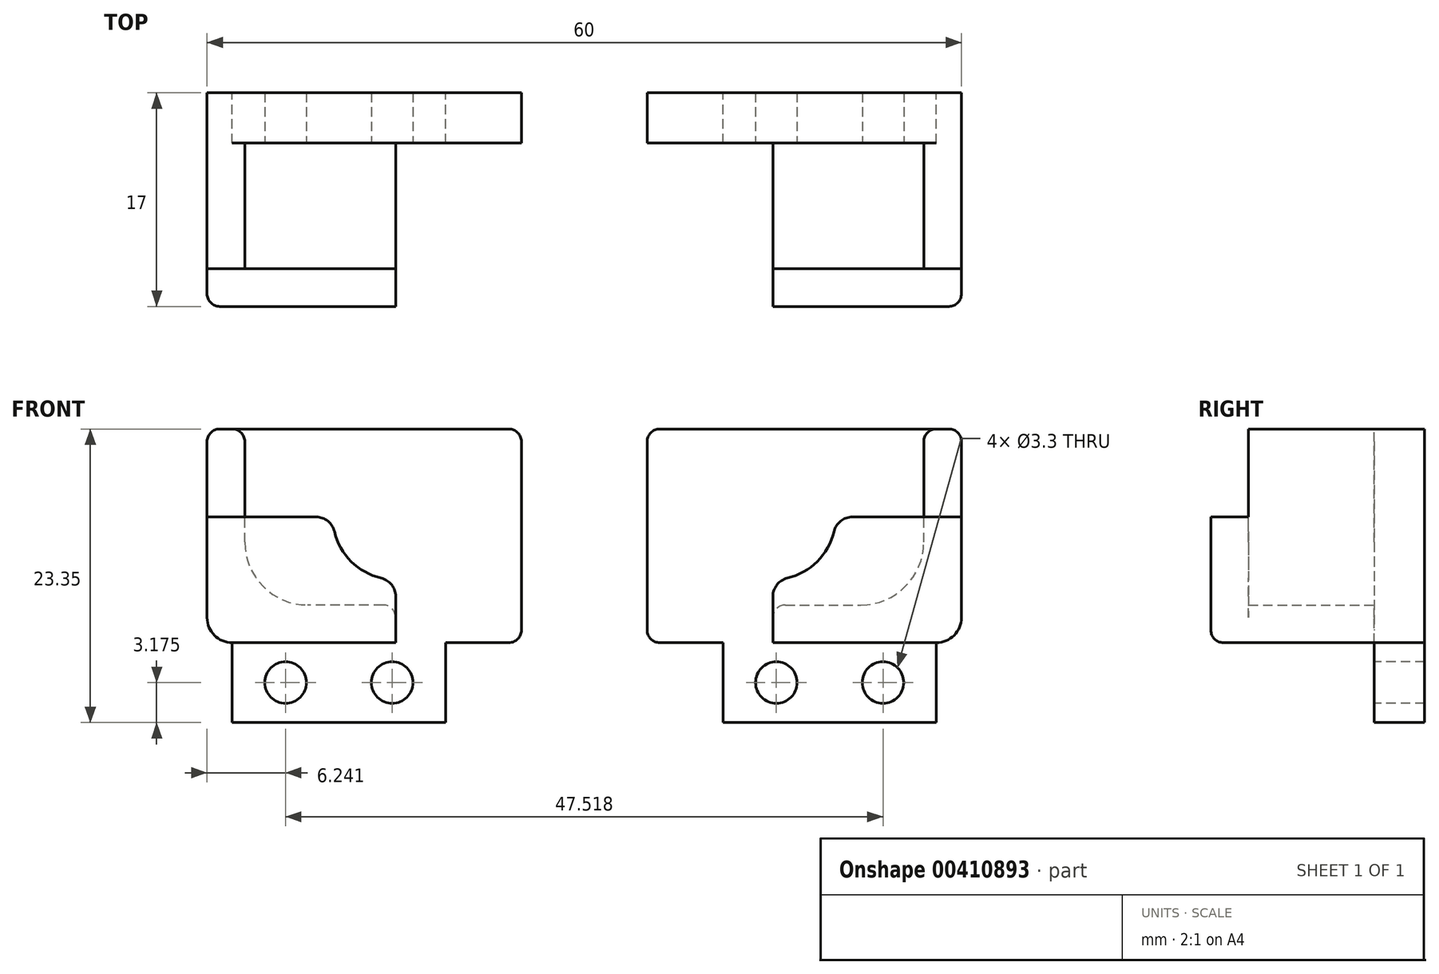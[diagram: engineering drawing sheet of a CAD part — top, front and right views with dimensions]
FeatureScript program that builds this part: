
annotation { "Feature Type Name" : "Feature", "Feature Type Description" : "" }
export const myFeature = defineFeature(function(context is Context, id is Id, definition is map)
    precondition{}
    {
        {
            var Q0;
            Q0=qCreatedBy(makeId("Top.planeOp"),FACE);
            var sketch = newSketch(context, id + "F0", { "sketchPlane" : qUnion([Q0])});
            skLineSegment(sketch, "E0.bottom", {"start": v(-25, 17) * mm, "end": v(0, 17) * mm});
            skLineSegment(sketch, "E0.top", {"start": v(-25, 0) * mm, "end": v(0, 0) * mm});
            skLineSegment(sketch, "E0.left", {"start": v(-25, 17) * mm, "end": v(-25, 0) * mm});
            skLineSegment(sketch, "E0.right", {"start": v(0, 17) * mm, "end": v(0, 0) * mm});
            skSolve(sketch);
        }
        {
            var Q0;
            Q0=makeQuery(id+"F0.imprint","IMPRINT",FACE,{"disambiguationData":[TD([[makeQuery(id+"F0.imprint","IMPRINT",EDGE,{"derivedFrom":sQuery(id+"F0.wireOp",EDGE,"E0.bottom")}),-1.0]])]});
            extrude(context, id + "F1", {"entities" : qUnion([Q0]), "depth" : 4 * mm});
        }
        {
            var Q0;
            Q0=makeQuery(id+"F1.opExtrude","CAP_FACE",FACE,{"disambiguationData":[OSD([sQuery(id+"F0.wireOp",EDGE,"E0.bottom"),sQuery(id+"F0.wireOp",EDGE,"E0.top"),sQuery(id+"F0.wireOp",EDGE,"E0.left"),sQuery(id+"F0.wireOp",EDGE,"E0.right")])],"isStart":false});
            var sketch = newSketch(context, id + "F2", { "sketchPlane" : qUnion([Q0])});
            skLineSegment(sketch, "E1", {"start": v(-25, 17) * mm, "end": v(-25, 0) * mm});
            skLineSegment(sketch, "E2", {"start": v(-25, 0) * mm, "end": v(-10, 0) * mm});
            skLineSegment(sketch, "E3", {"start": v(-10, 0) * mm, "end": v(-10, 3) * mm});
            skLineSegment(sketch, "E4", {"start": v(-10, 3) * mm, "end": v(-22, 3) * mm});
            skLineSegment(sketch, "E5", {"start": v(-22, 3) * mm, "end": v(-22, 17) * mm});
            skLineSegment(sketch, "E6", {"start": v(-22, 17) * mm, "end": v(-25, 17) * mm});
            skSolve(sketch);
        }
        {
            var Q0;
            Q0=makeQuery(id+"F2.imprint","IMPRINT",FACE,{"disambiguationData":[TD([[makeQuery(id+"F2.imprint","IMPRINT",EDGE,{"derivedFrom":sQuery(id+"F2.wireOp",EDGE,"E1")}),1.0]])]});
            extrude(context, id + "F3", {"entities" : qUnion([Q0]), "operationType" : NewBodyOperationType.ADD, "depth" : 10 * mm});
        }
        {
            var Q0;
            Q0=makeQuery(id+"F3.opExtrude","CAP_FACE",FACE,{"disambiguationData":[OSD([sQuery(id+"F2.wireOp",EDGE,"E1"),sQuery(id+"F2.wireOp",EDGE,"E2"),sQuery(id+"F2.wireOp",EDGE,"E3"),sQuery(id+"F2.wireOp",EDGE,"E4"),sQuery(id+"F2.wireOp",EDGE,"E5"),sQuery(id+"F2.wireOp",EDGE,"E6")])],"isStart":false});
            var sketch = newSketch(context, id + "F4", { "sketchPlane" : qUnion([Q0])});
            skLineSegment(sketch, "E7.bottom", {"start": v(-25, 10) * mm, "end": v(-16.32, 10) * mm});
            skLineSegment(sketch, "E7.top", {"start": v(-25, 0) * mm, "end": v(-10, 0) * mm});
            skLineSegment(sketch, "E7.left", {"start": v(-25, 10) * mm, "end": v(-25, 0) * mm});
            skLineSegment(sketch, "E7.right", {"start": v(-10, 10) * mm, "end": v(-10, 5) * mm, "construction": true});
            skArc(sketch, "E8", {"start": v(-14.87, 8.85) * mm, "mid": v(-13.54, 6.46) * mm, "end": v(-11.15, 5.13) * mm});
            skLineSegment(sketch, "E9", {"start": v(-15, 10) * mm, "end": v(-10, 10) * mm, "construction": true});
            skLineSegment(sketch, "E10", {"start": v(-10, 3.68) * mm, "end": v(-10, 0) * mm});
            skPoint(sketch, "E11.visualSharp", {"position": v(-15, 10) * mm});
            skArc(sketch, "E11.filletArc", {"start": v(-14.87, 8.85) * mm, "mid": v(-15.4, 9.68) * mm, "end": v(-16.32, 10) * mm});
            skPoint(sketch, "E12.visualSharp", {"position": v(-10, 5) * mm});
            skArc(sketch, "E12.filletArc", {"start": v(-10, 3.68) * mm, "mid": v(-10.32, 4.6) * mm, "end": v(-11.15, 5.13) * mm});
            skSolve(sketch);
        }
        {
            var Q0;
            {var subQ1=makeQuery(id+"F3.opExtrude","CAP_EDGE",EDGE,{"disambiguationData":[OSD([sQuery(id+"F2.wireOp",EDGE,"E4")])],"isStart":false});Q0=makeQuery(id+"F4.imprint","IMPRINT",FACE,{"disambiguationData":[TD([[makeQuery(id+"F4.imprint","IMPRINT",EDGE,{"derivedFrom":subQ1}),-1.0]])]});}
            var Q1;
            {var subQ4=sQuery(id+"F4.wireOp",EDGE,"E7.top");Q1=makeQuery(id+"F4.imprint","IMPRINT",FACE,{"disambiguationData":[TD([[makeQuery(id+"F4.imprint","IMPRINT",EDGE,{"derivedFrom":subQ4}),1.0]])]});}
            extrude(context, id + "F5", {"entities" : qUnion([Q0, Q1]), "operationType" : NewBodyOperationType.ADD, "depth" : 3 * mm});
        }
        {
            var Q0;
            Q0=makeQuery(id+"F3.opExtrude","SWEPT_EDGE",EDGE,{"disambiguationData":[OSD([sQuery(id+"F2.wireOp",EDGE,"E4"),sQuery(id+"F2.wireOp",EDGE,"E5")])]});
            fillet(context, id + "F6", {"entities" : qUnion([Q0]), "radius" : 5 * mm, "tangentPropagation" : true, "allowEdgeOverflow" : false});
        }
        {
            var Q0;
            Q0=makeQuery(id+"F1.opExtrude","SWEPT_BODY",BODY,{"disambiguationData":[OSD([sQuery(id+"F0.wireOp",EDGE,"E0.bottom"),sQuery(id+"F0.wireOp",EDGE,"E0.top"),sQuery(id+"F0.wireOp",EDGE,"E0.left"),sQuery(id+"F0.wireOp",EDGE,"E0.right")])]});
            var Q1;
            Q1=makeQuery(id+"F1.opExtrude","CAP_EDGE",EDGE,{"disambiguationData":[OSD([sQuery(id+"F0.wireOp",EDGE,"E0.top")])],"isStart":true});
            transform(context, id + "F7", {"entities" : qUnion([Q0]), "transformType" : TransformType.ROTATION, "transformAxis" : qUnion([Q1]), "angle" : 90 * degree, "makeCopy" : false});
        }
        {
            var Q0;
            Q0=makeQuery(id+"F1.opExtrude","SWEPT_EDGE",EDGE,{"disambiguationData":[OSD([sQuery(id+"F0.wireOp",EDGE,"E0.bottom"),sQuery(id+"F0.wireOp",EDGE,"E0.right")])]});
            var Q1;
            Q1=makeQuery(id+"F1.opExtrude","SWEPT_EDGE",EDGE,{"disambiguationData":[OSD([sQuery(id+"F0.wireOp",EDGE,"E0.top"),sQuery(id+"F0.wireOp",EDGE,"E0.right")])]});
            var Q2;
            Q2=makeQuery(id+"F5.opExtrude","SWEPT_EDGE",EDGE,{"disambiguationData":[OSD([sQuery(id+"F4.wireOp",EDGE,"E7.bottom"),sQuery(id+"F4.wireOp",EDGE,"E7.right")])]});
            var Q3;
            Q3=makeQuery(id+"F3.boolean.opBoolean","MERGE",EDGE,{"derivedFrom":[makeQuery(id+"F1.opExtrude","SWEPT_EDGE",EDGE,{"disambiguationData":[OSD([sQuery(id+"F0.wireOp",EDGE,"E0.bottom"),sQuery(id+"F0.wireOp",EDGE,"E0.left")])]}),makeQuery(id+"F3.opExtrude","SWEPT_EDGE",EDGE,{"disambiguationData":[OSD([sQuery(id+"F2.wireOp",EDGE,"E1"),sQuery(id+"F2.wireOp",EDGE,"E6")])]})]});
            var Q4;
            Q4=makeQuery(id+"F3.opExtrude","SWEPT_EDGE",EDGE,{"disambiguationData":[OSD([sQuery(id+"F0.wireOp",EDGE,"E0.bottom"),sQuery(id+"F2.wireOp",EDGE,"E5"),sQuery(id+"F2.wireOp",EDGE,"E6")])]});
            var Q5;
            Q5=makeQuery(id+"F3.opExtrude","SWEPT_EDGE",EDGE,{"disambiguationData":[OSD([sQuery(id+"F2.wireOp",EDGE,"E3"),sQuery(id+"F2.wireOp",EDGE,"E4")])]});
            var Q6;
            Q6=makeQuery(id+"F5.opExtrude","CAP_EDGE",EDGE,{"disambiguationData":[OSD([sQuery(id+"F4.wireOp",EDGE,"E7.left")])],"isStart":false});
            var Q7;
            Q7=makeQuery(id+"F5.opExtrude","CAP_EDGE",EDGE,{"disambiguationData":[OSD([sQuery(id+"F4.wireOp",EDGE,"E7.top")])],"isStart":false});
            fillet(context, id + "F8", {"entities" : qUnion([Q0, Q1, Q2, Q3, Q4, Q5, Q6, Q7]), "radius" : 1 * mm, "tangentPropagation" : true, "allowEdgeOverflow" : false});
        }
        {
            var Q0;
            Q0=makeQuery(id+"F5.boolean.opBoolean","MERGE",EDGE,{"derivedFrom":[makeQuery(id+"F3.boolean.opBoolean","MERGE",EDGE,{"derivedFrom":[makeQuery(id+"F1.opExtrude","SWEPT_EDGE",EDGE,{"disambiguationData":[OSD([sQuery(id+"F0.wireOp",EDGE,"E0.top"),sQuery(id+"F0.wireOp",EDGE,"E0.left")])]}),makeQuery(id+"F3.opExtrude","SWEPT_EDGE",EDGE,{"disambiguationData":[OSD([sQuery(id+"F2.wireOp",EDGE,"E1"),sQuery(id+"F2.wireOp",EDGE,"E2")])]})]}),makeQuery(id+"F5.opExtrude","SWEPT_EDGE",EDGE,{"disambiguationData":[OSD([sQuery(id+"F4.wireOp",EDGE,"E7.top"),sQuery(id+"F4.wireOp",EDGE,"E7.left")])]})]});
            fillet(context, id + "F9", {"entities" : qUnion([Q0]), "radius" : 2 * mm, "tangentPropagation" : true, "allowEdgeOverflow" : false});
        }
        {
            var Q0;
            Q0=makeQuery(id+"F1.opExtrude","SWEPT_BODY",BODY,{"disambiguationData":[OSD([sQuery(id+"F0.wireOp",EDGE,"E0.bottom"),sQuery(id+"F0.wireOp",EDGE,"E0.top"),sQuery(id+"F0.wireOp",EDGE,"E0.left"),sQuery(id+"F0.wireOp",EDGE,"E0.right")])]});
            var Q1;
            Q1=qCreatedBy(makeId("Right.planeOp"),FACE);
            transform(context, id + "F10", {"entities" : qUnion([Q0]), "transformType" : TransformType.TRANSLATION_DISTANCE, "transformDirection" : qUnion([Q1]), "distance" : 5 * mm, "oppositeDirection" : true, "makeCopy" : false});
        }
        {
            var Q0;
            Q0=makeQuery(id+"F5.boolean.opBoolean","MERGE",FACE,{"derivedFrom":[makeQuery(id+"F3.boolean.opBoolean","MERGE",FACE,{"derivedFrom":[makeQuery(id+"F1.opExtrude","SWEPT_FACE",FACE,{"disambiguationData":[OSD([sQuery(id+"F0.wireOp",EDGE,"E0.top")])]}),makeQuery(id+"F3.opExtrude","SWEPT_FACE",FACE,{"disambiguationData":[OSD([sQuery(id+"F2.wireOp",EDGE,"E2")])]})]}),makeQuery(id+"F5.opExtrude","SWEPT_FACE",FACE,{"disambiguationData":[OSD([sQuery(id+"F4.wireOp",EDGE,"E7.top")])]})]});
            var sketch = newSketch(context, id + "F11", { "sketchPlane" : qUnion([Q0])});
            skLineSegment(sketch, "E13.bottom", {"start": v(-11.04, 0) * mm, "end": v(-28, 0) * mm});
            skLineSegment(sketch, "E13.top", {"start": v(-11.04, 4) * mm, "end": v(-28, 4) * mm});
            skLineSegment(sketch, "E13.right", {"start": v(-28, 0) * mm, "end": v(-28, 4) * mm});
            skLineSegment(sketch, "E14", {"start": v(-11.04, 4) * mm, "end": v(-11.04, 0) * mm});
            skSolve(sketch);
        }
        {
            var Q0;
            Q0 = qSketchRegion(id + "F11", true);
            extrude(context, id + "F12", {"entities" : qUnion([Q0]), "operationType" : NewBodyOperationType.ADD, "depth" : 6.35 * mm});
        }
        {
            var Q0;
            Q0=makeQuery(id+"F12.boolean.opBoolean","MERGE",FACE,{"derivedFrom":[makeQuery(id+"F1.opExtrude","CAP_FACE",FACE,{"disambiguationData":[OSD([sQuery(id+"F0.wireOp",EDGE,"E0.bottom"),sQuery(id+"F0.wireOp",EDGE,"E0.top"),sQuery(id+"F0.wireOp",EDGE,"E0.left"),sQuery(id+"F0.wireOp",EDGE,"E0.right")])],"isStart":false}),makeQuery(id+"F12.opExtrude","SWEPT_FACE",FACE,{"disambiguationData":[OSD([sQuery(id+"F11.wireOp",EDGE,"E13.top")])]})]});
            var sketch = newSketch(context, id + "F13", { "sketchPlane" : qUnion([Q0])});
            skPoint(sketch, "E15.orphan", {"position": v(-11.04, -3.17) * mm});
            skCircle(sketch, "E16", {"center": v(-23.76, -3.18) * mm, "radius": 1.65 * mm});
            skCircle(sketch, "E17", {"center": v(-15.28, -3.17) * mm, "radius": 1.65 * mm});
            skPoint(sketch, "E18.end.orphan", {"position": v(-19.52, -6.35) * mm});
            skPoint(sketch, "E19.orphan", {"position": v(-19.52, -3.18) * mm});
            skPoint(sketch, "E20.orphan", {"position": v(-28, -3.18) * mm});
            skSolve(sketch);
        }
        {
            var Q0;
            Q0=makeQuery(id+"F13.imprint","IMPRINT",FACE,{"disambiguationData":[TD([[makeQuery(id+"F13.imprint","IMPRINT",EDGE,{"derivedFrom":sQuery(id+"F13.wireOp",EDGE,"E16")}),1.0]])]});
            var Q1;
            Q1=makeQuery(id+"F13.imprint","IMPRINT",FACE,{"disambiguationData":[TD([[makeQuery(id+"F13.imprint","IMPRINT",EDGE,{"derivedFrom":sQuery(id+"F13.wireOp",EDGE,"E17")}),1.0]])]});
            var Q2;
            Q2=sQuery(id+"F13.wireOp",EDGE,"E16");
            var Q3;
            Q3=sQuery(id+"F13.wireOp",EDGE,"E17");
            extrude(context, id + "F14", {"entities" : qUnion([Q0, Q1]), "operationType" : NewBodyOperationType.REMOVE, "surfaceEntities" : qUnion([Q2, Q3]), "oppositeDirection" : true, "depth" : 25 * mm});
        }
        {
            var Q0;
            Q0=makeQuery(id+"F1.opExtrude","SWEPT_BODY",BODY,{"disambiguationData":[OSD([sQuery(id+"F0.wireOp",EDGE,"E0.bottom"),sQuery(id+"F0.wireOp",EDGE,"E0.top"),sQuery(id+"F0.wireOp",EDGE,"E0.left"),sQuery(id+"F0.wireOp",EDGE,"E0.right")])]});
            var Q1;
            Q1=qCreatedBy(makeId("Right.planeOp"),FACE);
            mirror(context, id + "F15", {"entities" : qUnion([Q0]), "mirrorPlane" : qUnion([Q1])});
        }
    });
